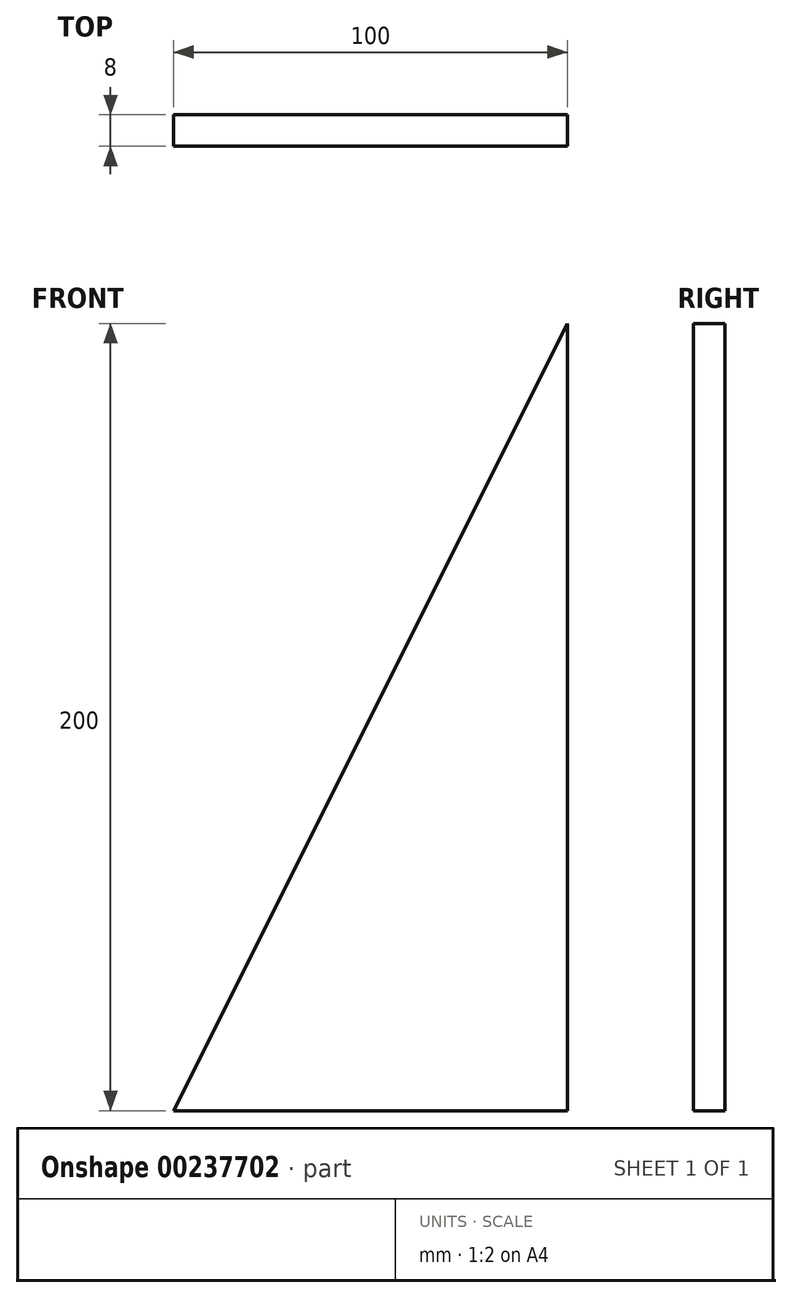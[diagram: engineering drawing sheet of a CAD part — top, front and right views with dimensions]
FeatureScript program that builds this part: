
annotation { "Feature Type Name" : "Feature", "Feature Type Description" : "" }
export const myFeature = defineFeature(function(context is Context, id is Id, definition is map)
    precondition{}
    {
        {
            var Q0;
            Q0=qCreatedBy(makeId("Front.planeOp"),FACE);
            var sketch = newSketch(context, id + "F0", { "sketchPlane" : qUnion([Q0])});
            skLineSegment(sketch, "E0.top", {"start": v(-50, -100) * mm, "end": v(50, -100) * mm});
            skLineSegment(sketch, "E0.right", {"start": v(50, 100) * mm, "end": v(50, -100) * mm});
            skPoint(sketch, "E0.middle", {"position": v(0, 0) * mm});
            skLineSegment(sketch, "E1", {"start": v(50, 100) * mm, "end": v(-50, -100) * mm});
            skPoint(sketch, "E0.left.start.orphan", {"position": v(-50, 100) * mm});
            skSolve(sketch);
        }
        {
            var Q0;
            Q0=makeQuery(id+"F0.imprint","IMPRINT",FACE,{"disambiguationData":[TD([[makeQuery(id+"F0.imprint","IMPRINT",EDGE,{"derivedFrom":sQuery(id+"F0.wireOp",EDGE,"E0.top")}),1.0]])]});
            extrude(context, id + "F1", {"entities" : qUnion([Q0]), "depth" : 8 * mm});
        }
    });
